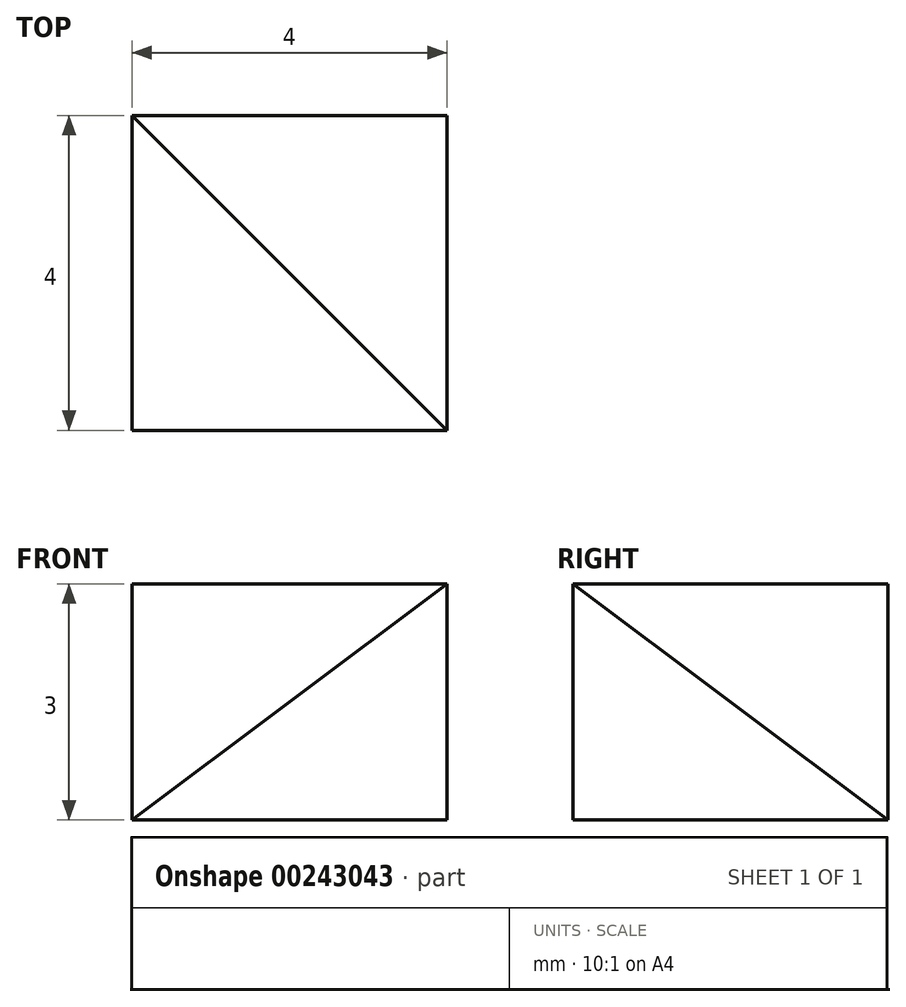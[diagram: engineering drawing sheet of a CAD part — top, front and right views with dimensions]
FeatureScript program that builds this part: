
annotation { "Feature Type Name" : "Feature", "Feature Type Description" : "" }
export const myFeature = defineFeature(function(context is Context, id is Id, definition is map)
    precondition{}
    {
        {
            var Q0;
            Q0=qCreatedBy(makeId("Top.planeOp"),FACE);
            var sketch = newSketch(context, id + "F0", { "sketchPlane" : qUnion([Q0])});
            skLineSegment(sketch, "E0.bottom", {"start": v(0, 0) * mm, "end": v(4, 0) * mm});
            skLineSegment(sketch, "E0.top", {"start": v(0, 4) * mm, "end": v(4, 4) * mm});
            skLineSegment(sketch, "E0.left", {"start": v(0, 0) * mm, "end": v(0, 4) * mm});
            skLineSegment(sketch, "E0.right", {"start": v(4, 0) * mm, "end": v(4, 4) * mm});
            skSolve(sketch);
        }
        {
            var Q0;
            Q0 = qSketchRegion(id + "F0", true);
            extrude(context, id + "F1", {"entities" : qUnion([Q0]), "depth" : 3 * mm});
        }
        {
            var Q0;
            Q0=makeQuery(id+"F1.opExtrude","CAP_VERTEX",VERTEX,{"disambiguationData":[OSD([sQuery(id+"F0.wireOp",EDGE,"E0.top"),sQuery(id+"F0.wireOp",EDGE,"E0.left")])],"isStart":false});
            var Q1;
            Q1=makeQuery(id+"F1.opExtrude","CAP_VERTEX",VERTEX,{"disambiguationData":[OSD([sQuery(id+"F0.wireOp",EDGE,"E0.bottom"),sQuery(id+"F0.wireOp",EDGE,"E0.right")])],"isStart":false});
            var Q2;
            Q2=qCreatedBy(makeId("Origin.pointOp"),VERTEX);
            cPlane(context, id + "F2", {"entities" : qUnion([Q0, Q1, Q2]), "cplaneType" : CPlaneType.THREE_POINT, "offset" : 25 * mm, "width" : 150 * mm, "height" : 150 * mm});
        }
        {
            var Q0;
            Q0=qCreatedBy(id+"F2.planeOp",FACE);
            var sketch = newSketch(context, id + "F3", { "sketchPlane" : qUnion([Q0])});
            skLineSegment(sketch, "E1.bottom", {"start": v(-4.05, 6.14) * mm, "end": v(10.28, 6.14) * mm});
            skLineSegment(sketch, "E1.top", {"start": v(-4.05, -4.53) * mm, "end": v(10.28, -4.53) * mm});
            skLineSegment(sketch, "E1.left", {"start": v(-4.05, 6.14) * mm, "end": v(-4.05, -4.53) * mm});
            skLineSegment(sketch, "E1.right", {"start": v(10.28, 6.14) * mm, "end": v(10.28, -4.53) * mm});
            skSolve(sketch);
        }
        {
            var Q0;
            Q0 = qSketchRegion(id + "F3", true);
            extrude(context, id + "F4", {"entities" : qUnion([Q0]), "operationType" : NewBodyOperationType.REMOVE, "depth" : 25 * mm});
        }
        {
            var Q0;
            Q0=makeQuery(id+"F1.opExtrude","CAP_VERTEX",VERTEX,{"disambiguationData":[OSD([sQuery(id+"F0.wireOp",EDGE,"E0.top"),sQuery(id+"F0.wireOp",EDGE,"E0.left")])],"isStart":false});
            var Q1;
            Q1=makeQuery(id+"F1.opExtrude","CAP_VERTEX",VERTEX,{"disambiguationData":[OSD([sQuery(id+"F0.wireOp",EDGE,"E0.top"),sQuery(id+"F0.wireOp",EDGE,"E0.right")])],"isStart":true});
            var Q2;
            Q2=makeQuery(id+"F1.opExtrude","CAP_VERTEX",VERTEX,{"disambiguationData":[OSD([sQuery(id+"F0.wireOp",EDGE,"E0.bottom"),sQuery(id+"F0.wireOp",EDGE,"E0.right")])],"isStart":false});
            cPlane(context, id + "F5", {"entities" : qUnion([Q0, Q1, Q2]), "cplaneType" : CPlaneType.THREE_POINT, "offset" : 25 * mm, "width" : 150 * mm, "height" : 150 * mm});
        }
        {
            var Q0;
            Q0=qCreatedBy(id+"F5.planeOp",FACE);
            var sketch = newSketch(context, id + "F6", { "sketchPlane" : qUnion([Q0])});
            skLineSegment(sketch, "E2.bottom", {"start": v(-6.64, -8.99) * mm, "end": v(10.6, -8.99) * mm});
            skLineSegment(sketch, "E2.top", {"start": v(-6.64, 13.16) * mm, "end": v(10.6, 13.16) * mm});
            skLineSegment(sketch, "E2.left", {"start": v(-6.64, -8.99) * mm, "end": v(-6.64, 13.16) * mm});
            skLineSegment(sketch, "E2.right", {"start": v(10.6, -8.99) * mm, "end": v(10.6, 13.16) * mm});
            skSolve(sketch);
        }
        {
            var Q0;
            Q0 = qSketchRegion(id + "F6", true);
            extrude(context, id + "F7", {"entities" : qUnion([Q0]), "operationType" : NewBodyOperationType.REMOVE, "depth" : 25 * mm});
        }
    });
